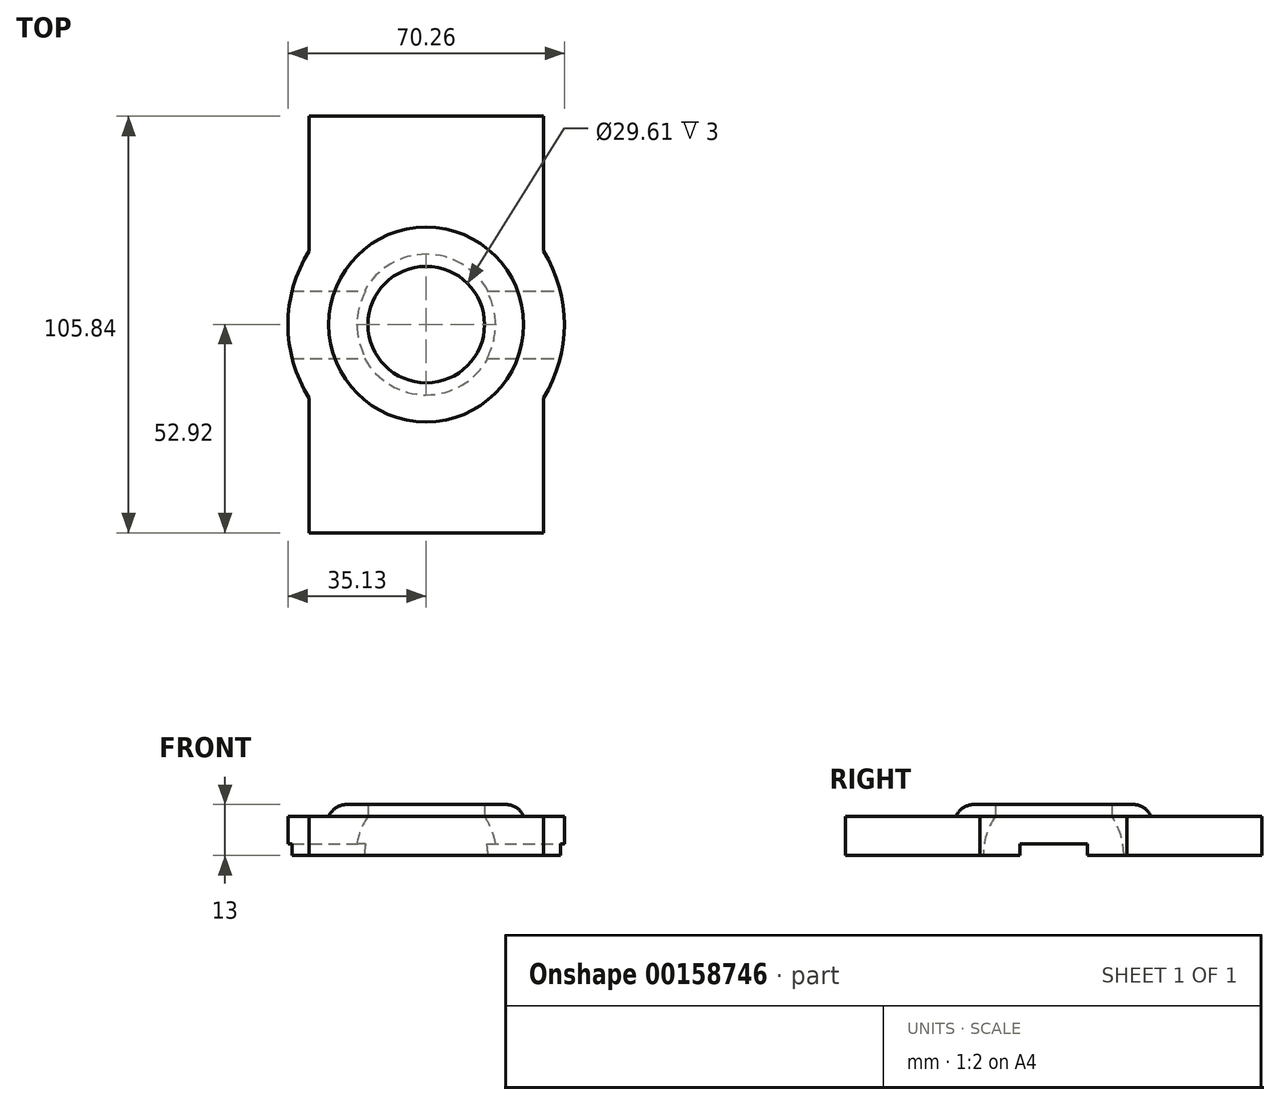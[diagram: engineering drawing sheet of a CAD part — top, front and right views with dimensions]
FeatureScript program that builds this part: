
annotation { "Feature Type Name" : "Feature", "Feature Type Description" : "" }
export const myFeature = defineFeature(function(context is Context, id is Id, definition is map)
    precondition{}
    {
        {
            var Q0;
            Q0=qCreatedBy(makeId("Top.planeOp"),FACE);
            var sketch = newSketch(context, id + "F0", { "sketchPlane" : qUnion([Q0])});
            skLineSegment(sketch, "E0.bottom", {"start": v(-29.76, -52.92) * mm, "end": v(29.76, -52.92) * mm});
            skLineSegment(sketch, "E0.top", {"start": v(-29.76, 52.92) * mm, "end": v(29.76, 52.92) * mm});
            skLineSegment(sketch, "E0.left", {"start": v(-29.76, -52.92) * mm, "end": v(-29.76, 52.92) * mm});
            skLineSegment(sketch, "E0.right", {"start": v(29.76, -52.92) * mm, "end": v(29.76, 52.92) * mm});
            skPoint(sketch, "E0.middle", {"position": v(0, 0) * mm});
            skCircle(sketch, "E1", {"center": v(0, 0) * mm, "radius": 35.13 * mm});
            skSolve(sketch);
        }
        {
            var Q0;
            Q0 = qSketchRegion(id + "F0", true);
            extrude(context, id + "F1", {"entities" : qUnion([Q0]), "depth" : 10 * mm});
        }
        {
            var Q0;
            Q0=qCreatedBy(makeId("Top.planeOp"),FACE);
            var sketch = newSketch(context, id + "F2", { "sketchPlane" : qUnion([Q0])});
            skLineSegment(sketch, "E2.bottom", {"start": v(-39.59, 8.56) * mm, "end": v(39.59, 8.56) * mm});
            skLineSegment(sketch, "E2.top", {"start": v(-39.59, -8.56) * mm, "end": v(39.59, -8.56) * mm});
            skLineSegment(sketch, "E2.left", {"start": v(-39.59, 8.56) * mm, "end": v(-39.59, -8.56) * mm});
            skLineSegment(sketch, "E2.right", {"start": v(39.59, 8.56) * mm, "end": v(39.59, -8.56) * mm});
            skPoint(sketch, "E2.middle", {"position": v(0, 0) * mm});
            skSolve(sketch);
        }
        {
            var Q0;
            Q0 = qSketchRegion(id + "F2", true);
            extrude(context, id + "F3", {"entities" : qUnion([Q0]), "operationType" : NewBodyOperationType.REMOVE, "depth" : 3 * mm});
        }
        {
            var Q0;
            Q0=qCreatedBy(makeId("Front.planeOp"),FACE);
            var sketch = newSketch(context, id + "F4", { "sketchPlane" : qUnion([Q0])});
            skCircle(sketch, "E3", {"center": v(0, 0) * mm, "radius": 17.86 * mm});
            skLineSegment(sketch, "E4", {"start": v(0, -28.52) * mm, "end": v(0, 33.75) * mm});
            skSolve(sketch);
        }
        {
            var Q0;
            {var subQ0=sQuery(id+"F4.wireOp",EDGE,"E4");var subQ1=sQuery(id+"F4.wireOp",EDGE,"E3");var subQ2=makeQuery(id+"F4.imprint","INTERSECT",VERTEX,{"disambiguationData":[OD(0.0)],"derivedFrom":[subQ1,subQ0]});Q0=makeQuery(id+"F4.imprint","IMPRINT",FACE,{"disambiguationData":[TD([[makeQuery(id+"F4.imprint","IMPRINT",EDGE,{"disambiguationData":[TD([[subQ2,-1.0]])],"derivedFrom":subQ1}),1.0]])]});}
            var Q1;
            Q1=sQuery(id+"F4.wireOp",EDGE,"E4");
            revolve(context, id + "F5", {"operationType" : NewBodyOperationType.REMOVE, "entities" : qUnion([Q0]), "axis" : qUnion([Q1]), "revolveType" : RevolveType.FULL, "oppositeDirection" : true});
        }
        {
            var Q0;
            Q0=makeQuery(id+"F1.opExtrude","CAP_FACE",FACE,{"disambiguationData":[OSD([sQuery(id+"F0.wireOp",EDGE,"E0.bottom"),sQuery(id+"F0.wireOp",EDGE,"E0.top"),sQuery(id+"F0.wireOp",EDGE,"E0.left"),sQuery(id+"F0.wireOp",EDGE,"E0.right"),sQuery(id+"F0.wireOp",EDGE,"E1")])],"isStart":false});
            var sketch = newSketch(context, id + "F6", { "sketchPlane" : qUnion([Q0])});
            skCircle(sketch, "E5", {"center": v(0, 0) * mm, "radius": 24.75 * mm});
            skSolve(sketch);
        }
        {
            var Q0;
            Q0=makeQuery(id+"F6.imprint","IMPRINT",FACE,{"disambiguationData":[TD([[makeQuery(id+"F6.imprint","IMPRINT",EDGE,{"derivedFrom":sQuery(id+"F6.wireOp",EDGE,"E5")}),1.0]])]});
            extrude(context, id + "F7", {"entities" : qUnion([Q0]), "operationType" : NewBodyOperationType.ADD, "depth" : 3 * mm});
        }
        {
            var Q0;
            Q0=makeQuery(id+"F7.opExtrude","CAP_EDGE",EDGE,{"disambiguationData":[OSD([sQuery(id+"F6.wireOp",EDGE,"E5")])],"isStart":false});
            fillet(context, id + "F8", {"entities" : qUnion([Q0]), "radius" : 5 * mm, "tangentPropagation" : true, "allowEdgeOverflow" : false});
        }
    });
